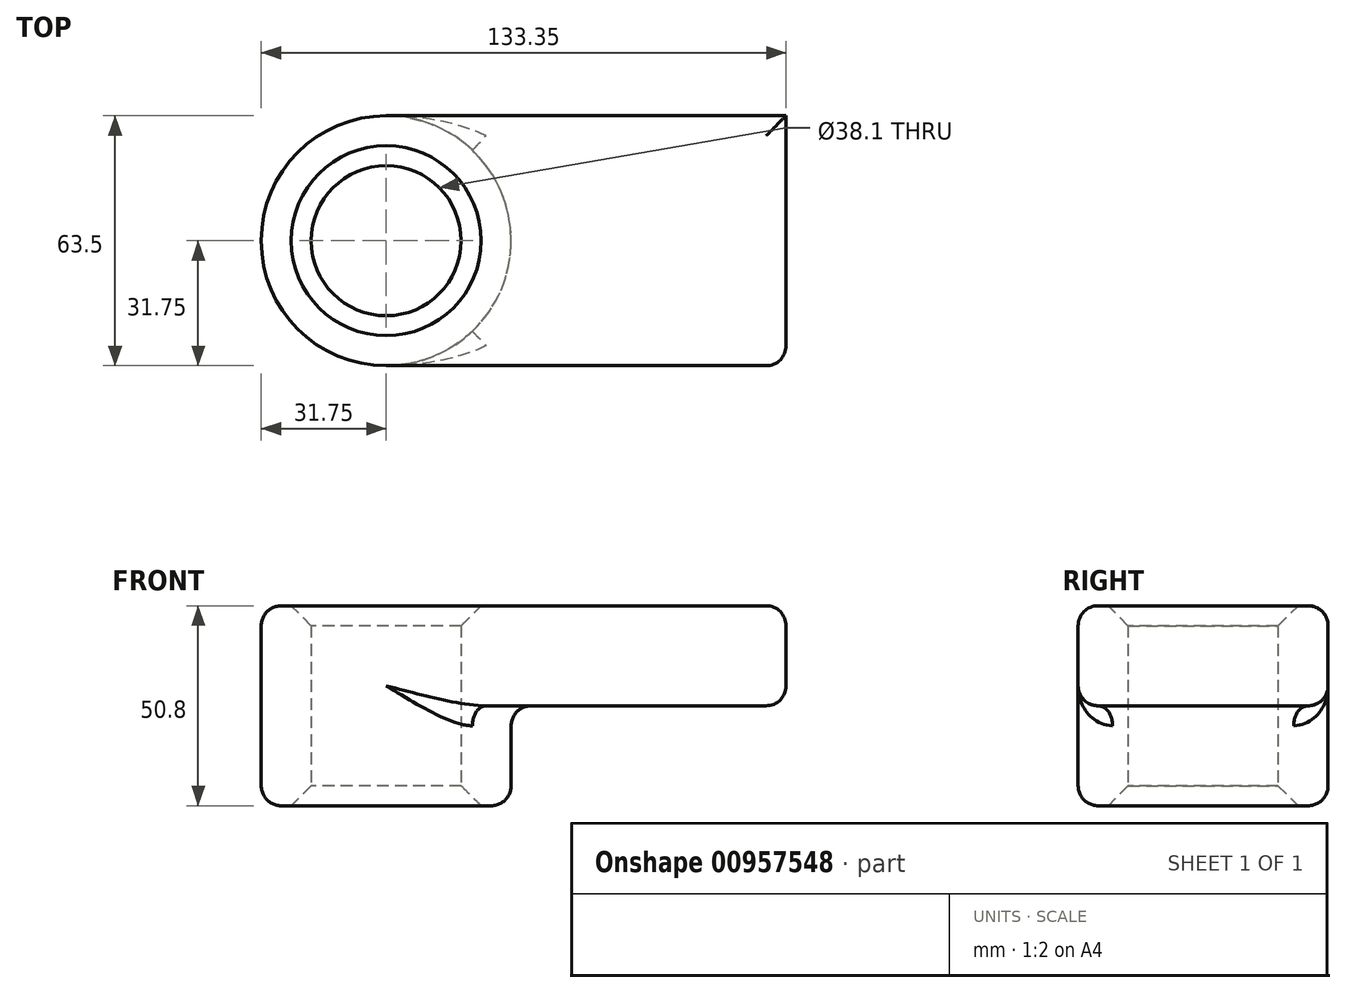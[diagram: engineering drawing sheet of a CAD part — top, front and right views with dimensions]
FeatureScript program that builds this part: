
annotation { "Feature Type Name" : "Feature", "Feature Type Description" : "" }
export const myFeature = defineFeature(function(context is Context, id is Id, definition is map)
    precondition{}
    {
        {
            var Q0;
            Q0=qCreatedBy(makeId("Top.planeOp"),FACE);
            var sketch = newSketch(context, id + "F0", { "sketchPlane" : qUnion([Q0])});
            skLineSegment(sketch, "E0.bottom", {"start": v(-50.8, 31.75) * mm, "end": v(50.8, 31.75) * mm});
            skLineSegment(sketch, "E0.top", {"start": v(-50.8, -31.75) * mm, "end": v(50.8, -31.75) * mm});
            skLineSegment(sketch, "E0.left", {"start": v(-50.8, 31.75) * mm, "end": v(-50.8, -31.75) * mm});
            skLineSegment(sketch, "E0.right", {"start": v(50.8, 31.75) * mm, "end": v(50.8, -31.75) * mm});
            skPoint(sketch, "E0.middle", {"position": v(0, 0) * mm});
            skCircle(sketch, "E1", {"center": v(-50.8, 0) * mm, "radius": 31.75 * mm});
            skCircle(sketch, "E2", {"center": v(-50.8, 0) * mm, "radius": 19.05 * mm});
            skSolve(sketch);
        }
        {
            var Q0;
            Q0 = qSketchRegion(id + "F0", true);
            extrude(context, id + "F1", {"entities" : qUnion([Q0]), "depth" : 25.4 * mm, "offsetDistance" : 25.4 * mm});
        }
        {
            var Q0;
            {var subQ1=sQuery(id+"F0.wireOp",EDGE,"E0.left");var subQ3=sQuery(id+"F0.wireOp",EDGE,"E2");var subQ4=makeQuery(id+"F0.imprint","INTERSECT",VERTEX,{"disambiguationData":[OD(0.0)],"derivedFrom":[subQ1,subQ3]});Q0=makeQuery(id+"F0.imprint","IMPRINT",FACE,{"disambiguationData":[TD([[makeQuery(id+"F0.imprint","IMPRINT",EDGE,{"disambiguationData":[TD([[subQ4,1.0]])],"derivedFrom":subQ3}),-1.0]])]});}
            var Q1;
            {var subQ1=sQuery(id+"F0.wireOp",EDGE,"E0.left");var subQ3=sQuery(id+"F0.wireOp",EDGE,"E2");var subQ4=makeQuery(id+"F0.imprint","INTERSECT",VERTEX,{"disambiguationData":[OD(0.0)],"derivedFrom":[subQ1,subQ3]});Q1=makeQuery(id+"F0.imprint","IMPRINT",FACE,{"disambiguationData":[TD([[makeQuery(id+"F0.imprint","IMPRINT",EDGE,{"disambiguationData":[TD([[subQ4,-1.0]])],"derivedFrom":subQ3}),-1.0]])]});}
            extrude(context, id + "F2", {"entities" : qUnion([Q0, Q1]), "operationType" : NewBodyOperationType.ADD, "oppositeDirection" : true, "depth" : 25.4 * mm, "offsetDistance" : 25.4 * mm});
        }
        {
            var Q0;
            Q0=makeQuery(id+"F1.opExtrude","CAP_EDGE",EDGE,{"disambiguationData":[OSD([sQuery(id+"F0.wireOp",EDGE,"E0.right")])],"isStart":false});
            var Q1;
            Q1=makeQuery(id+"F1.opExtrude","SWEPT_EDGE",EDGE,{"disambiguationData":[OSD([sQuery(id+"F0.wireOp",EDGE,"E0.top"),sQuery(id+"F0.wireOp",EDGE,"E0.right")])]});
            var Q2;
            Q2=makeQuery(id+"F1.opExtrude","CAP_EDGE",EDGE,{"disambiguationData":[OSD([sQuery(id+"F0.wireOp",EDGE,"E0.top")])],"isStart":false});
            var Q3;
            Q3=makeQuery(id+"F2.opExtrude","CAP_EDGE",EDGE,{"disambiguationData":[OSD([sQuery(id+"F0.wireOp",EDGE,"E1")])],"isStart":true});
            var Q4;
            Q4=makeQuery(id+"F2.opExtrude","CAP_EDGE",EDGE,{"disambiguationData":[OSD([sQuery(id+"F0.wireOp",EDGE,"E1")])],"isStart":false});
            var Q5;
            Q5=makeQuery(id+"F1.opExtrude","CAP_EDGE",EDGE,{"disambiguationData":[OSD([sQuery(id+"F0.wireOp",EDGE,"E0.bottom")])],"isStart":true});
            var Q6;
            Q6=makeQuery(id+"F1.opExtrude","CAP_EDGE",EDGE,{"disambiguationData":[OSD([sQuery(id+"F0.wireOp",EDGE,"E0.right")])],"isStart":true});
            var Q7;
            Q7=makeQuery(id+"F1.opExtrude","CAP_EDGE",EDGE,{"disambiguationData":[OSD([sQuery(id+"F0.wireOp",EDGE,"E0.top")])],"isStart":true});
            fillet(context, id + "F3", {"entities" : qUnion([Q0, Q1, Q2, Q3, Q4, Q5, Q6, Q7]), "radius" : 5.08 * mm, "tangentPropagation" : true, "allowEdgeOverflow" : false});
        }
        {
            var Q0;
            Q0=makeQuery(id+"F1.opExtrude","CAP_EDGE",EDGE,{"disambiguationData":[OSD([sQuery(id+"F0.wireOp",EDGE,"E2")])],"isStart":false});
            var Q1;
            Q1=makeQuery(id+"F2.opExtrude","CAP_EDGE",EDGE,{"disambiguationData":[OSD([sQuery(id+"F0.wireOp",EDGE,"E2")])],"isStart":false});
            chamfer(context, id + "F4", {"entities" : qUnion([Q0, Q1]), "width" : 5.08 * mm, "tangentPropagation" : true});
        }
    });
